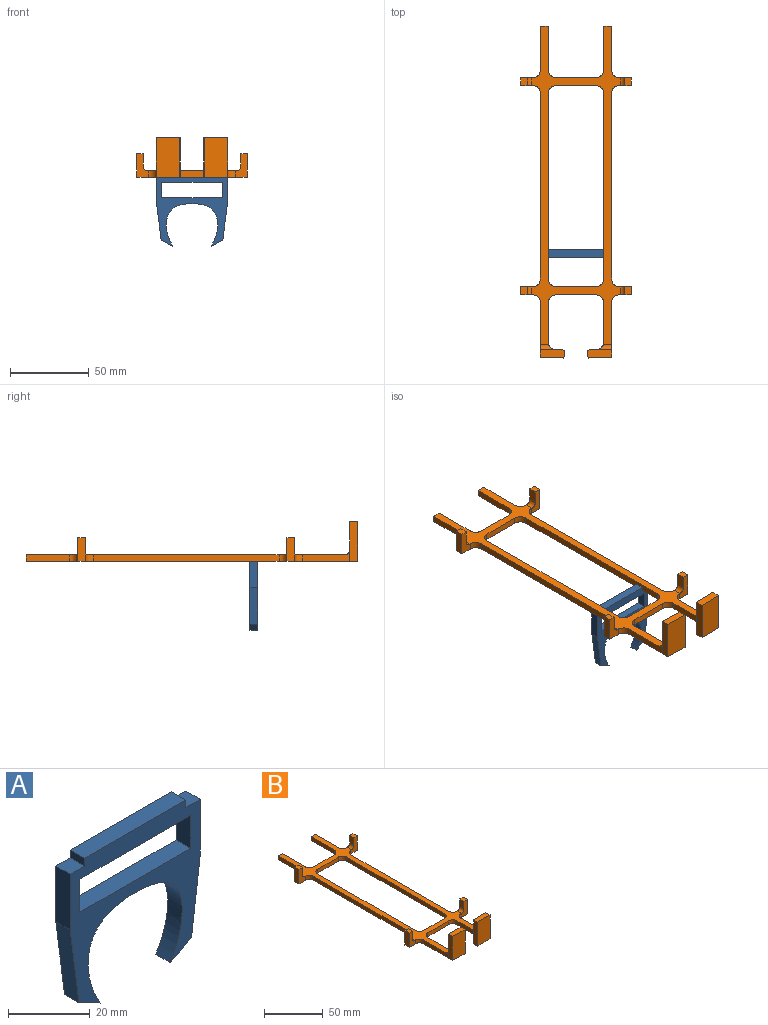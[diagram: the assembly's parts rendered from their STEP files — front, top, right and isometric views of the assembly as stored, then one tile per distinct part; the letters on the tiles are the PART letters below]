
ASSEMBLY  parts=2 mates=1
PART A: 19 faces, bbox 45x5x46.1 mm
  f0: plane 46.06x45mm, normal (0,-1,0), area 782mm2, adj f2,f3,f4,f5,f6,f7,f8,f9
  f1: plane 46.06x45mm, normal (0,1,0), area 782mm2, adj f2,f3,f4,f5,f6,f7,f8,f9
  f2: plane 35x5mm, normal (0,0,1), area 175mm2, adj f0,f1,f12,f13
  f3: plane 23.26x5mm, normal (0.99,0,-0.13), area 117.3mm2, adj f0,f1,f4,f10
  f4: plane 16.71x5mm, normal (1,0,0), area 83.5mm2, adj f0,f1,f3,f14
  f5: plane 16.71x5mm, normal (-1,0,0), area 83.5mm2, adj f0,f1,f6,f11
  f6: plane 23.26x5mm, normal (-0.99,0,-0.13), area 117.3mm2, adj f0,f1,f5,f7
  f7: plane 7.38x5mm, normal (-0.46,0,-0.89), area 41.5mm2, adj f0,f1,f6,f8
  f8: extruded ~27.06x16.25mm, area 192.7mm2, adj f0,f1,f7,f9
  f9: extruded ~27.06x16.25mm, area 192.7mm2, adj f0,f1,f8,f10
  f10: plane 7.38x5mm, normal (0.46,0,-0.89), area 41.5mm2, adj f0,f1,f3,f9
  f11: plane 5x5mm, normal (0,0,1), area 25mm2, adj f0,f1,f5,f12
  f12: plane 5x2.29mm, normal (-1,0,0), area 11.5mm2, adj f0,f1,f2,f11
  f13: plane 5x2.29mm, normal (1,0,0), area 11.5mm2, adj f0,f1,f2,f14
  f14: plane 5x5mm, normal (0,0,1), area 25mm2, adj f0,f1,f4,f13
  f15: plane 38.33x5mm, normal (0,0,1), area 191.6mm2, adj f0,f1,f16,f18
  f16: plane 9.87x5mm, normal (-1,0,0), area 49.3mm2, adj f0,f1,f15,f17
  f17: plane 38.33x5mm, normal (0,0,-1), area 191.6mm2, adj f0,f1,f16,f18
  f18: plane 9.87x5mm, normal (1,0,0), area 49.3mm2, adj f0,f1,f15,f17
PART B: 74 faces, bbox 70x210.4x25 mm
  f0: plane 25x4mm, normal (0,1,0), area 100mm2, adj f26,f27,f56,f66
  f1: plane 117.57x4mm, normal (1,0,0), area 470.3mm2, adj f26,f27,f56,f57
  f2: plane 25x4mm, normal (0,-1,0), area 100mm2, adj f26,f27,f57,f62
  f3: plane 117.57x4mm, normal (-1,0,0), area 470.3mm2, adj f26,f27,f58,f59
  f4: plane 15x7.5mm, normal (0,1,0), area 75.9mm2, adj f26,f27,f44,f45,f46,f55,f59
  f5: plane 15x7.5mm, normal (0,-1,0), area 75.9mm2, adj f26,f27,f44,f45,f46,f55,f72
  f6: plane 29.73x7.03mm, normal (-1,0,0), area 120.7mm2, adj f26,f27,f28,f54,f72
  f7: plane 24.93x4mm, normal (1,0,0), area 99.7mm2, adj f26,f27,f71,f73
  f8: plane 25x4mm, normal (0,-1,0), area 100mm2, adj f26,f27,f69,f71
  f9: plane 24.93x4mm, normal (-1,0,0), area 99.7mm2, adj f26,f27,f69,f70
  f10: plane 29.73x7.03mm, normal (1,0,0), area 120.7mm2, adj f26,f27,f33,f52,f68
  f11: plane 15x7.5mm, normal (0,-1,0), area 75.9mm2, adj f26,f27,f38,f39,f40,f51,f68
  f12: plane 15x7.5mm, normal (0,1,0), area 75.9mm2, adj f26,f27,f38,f39,f40,f51,f67
  f13: plane 117.57x4mm, normal (1,0,0), area 470.3mm2, adj f26,f27,f65,f67
  f14: plane 15x7.5mm, normal (0,-1,0), area 75.9mm2, adj f26,f27,f41,f42,f43,f50,f65
  f15: plane 15x7.5mm, normal (0,1,0), area 75.9mm2, adj f26,f27,f41,f42,f43,f50,f64
  f16: plane 27.73x4mm, normal (1,0,0), area 110.9mm2, adj f17,f26,f27,f64
  f17: plane 5x4mm, normal (0,1,0), area 20mm2, adj f16,f18,f26,f27
  f18: plane 27.73x4mm, normal (-1,0,0), area 110.9mm2, adj f17,f26,f27,f63
  f19: plane 25x4mm, normal (0,1,0), area 100mm2, adj f26,f27,f60,f63
  f20: plane 27.73x4mm, normal (1,0,0), area 110.9mm2, adj f21,f26,f27,f60
  f21: plane 5x4mm, normal (0,1,0), area 20mm2, adj f20,f22,f26,f27
  f22: plane 27.73x4mm, normal (-1,0,0), area 110.9mm2, adj f21,f26,f27,f61
  f23: plane 15x7.5mm, normal (0,1,0), area 75.9mm2, adj f26,f27,f47,f48,f49,f53,f61
  f24: plane 15x7.5mm, normal (0,-1,0), area 75.9mm2, adj f26,f27,f47,f48,f49,f53,f58
  f25: plane 117.57x4mm, normal (-1,0,0), area 470.3mm2, adj f26,f27,f62,f66
  f26: plane 202.12x56mm, normal (0,0,1), area 2566.4mm2, adj f0,f1,f2,f3,f4,f5,f6,f7
  f27: plane 210.35x70mm, normal (0,0,-1), area 2896.1mm2, adj f0,f1,f2,f3,f4,f5,f6,f7
  f28: plane 25x5mm, normal (-1,0.02,0), area 125mm2, adj f6,f27,f30,f31,f32
  f29: plane 25x5mm, normal (1,-0.02,0), area 125mm2, adj f27,f30,f31,f32
  f30: plane 15.11x5.35mm, normal (0,0,1), area 75mm2, adj f28,f29,f31,f32
  f31: plane 25x15mm, normal (-0.02,-1,0), area 375mm2, adj f27,f28,f29,f30
  f32: plane 25x15mm, normal (0.02,1,0), area 305.8mm2, adj f27,f28,f29,f30,f54,f73
  f33: plane 25x5mm, normal (1,0.02,0), area 125mm2, adj f10,f27,f34,f36,f37
  f34: plane 15.11x5.35mm, normal (0,0,1), area 75mm2, adj f33,f35,f36,f37
  f35: plane 25x5mm, normal (-1,-0.02,0), area 125mm2, adj f27,f34,f36,f37
  f36: plane 25x15mm, normal (0.02,-1,0), area 375mm2, adj f27,f33,f34,f35
  f37: plane 25x15mm, normal (-0.02,1,0), area 305.8mm2, adj f27,f33,f34,f35,f52,f70
  f38: plane 8x5mm, normal (-1,0,0), area 40mm2, adj f11,f12,f39,f51
  f39: plane 5x4mm, normal (0,0,1), area 20mm2, adj f11,f12,f38,f40
  f40: plane 15x5mm, normal (1,0,0), area 75mm2, adj f11,f12,f27,f39
  f41: plane 8x5mm, normal (-1,0,0), area 40mm2, adj f14,f15,f42,f50
  f42: plane 5x4mm, normal (0,0,1), area 20mm2, adj f14,f15,f41,f43
  f43: plane 15x5mm, normal (1,0,0), area 75mm2, adj f14,f15,f27,f42
  f44: plane 5x4mm, normal (0,0,1), area 20mm2, adj f4,f5,f45,f46
  f45: plane 15x5mm, normal (-1,0,0), area 75mm2, adj f4,f5,f27,f44
  f46: plane 8x5mm, normal (1,0,0), area 40mm2, adj f4,f5,f44,f55
  f47: plane 5x4mm, normal (0,0,1), area 20mm2, adj f23,f24,f48,f49
  f48: plane 15x5mm, normal (-1,0,0), area 75mm2, adj f23,f24,f27,f47
  f49: plane 8x5mm, normal (1,0,0), area 40mm2, adj f23,f24,f47,f53
  f50: cylinder r=3mm len=5mm, axis (0,-1,0), area 23.6mm2, adj f14,f15,f26,f41
  f51: cylinder r=3mm len=5mm, axis (0,-1,0), area 23.6mm2, adj f11,f12,f26,f38
  f52: cylinder r=3mm len=10.02mm, axis (1,0.02,0), area 34.3mm2, adj f10,f26,f37,f70
  f53: cylinder r=3mm len=5mm, axis (0,-1,0), area 23.6mm2, adj f23,f24,f26,f49
  f54: cylinder r=3mm len=10.02mm, axis (-1,0.02,0), area 34.3mm2, adj f6,f26,f32,f73
  f55: cylinder r=3mm len=5mm, axis (0,-1,0), area 23.6mm2, adj f4,f5,f26,f46
  f56: cylinder r=5mm len=5mm, axis (0,0,1), area 31.4mm2, adj f0,f1,f26,f27
  f57: cylinder r=5mm len=5mm, axis (0,0,-1), area 31.4mm2, adj f1,f2,f26,f27
  f58: cylinder r=5mm len=5mm, axis (0,0,-1), area 31.4mm2, adj f3,f24,f26,f27
  f59: cylinder r=5mm len=5mm, axis (0,0,1), area 31.4mm2, adj f3,f4,f26,f27
  f60: cylinder r=5mm len=5mm, axis (0,0,1), area 31.4mm2, adj f19,f20,f26,f27
  f61: cylinder r=5mm len=5mm, axis (0,0,1), area 31.4mm2, adj f22,f23,f26,f27
  f62: cylinder r=5mm len=5mm, axis (0,0,1), area 31.4mm2, adj f2,f25,f26,f27
  f63: cylinder r=5mm len=5mm, axis (0,0,-1), area 31.4mm2, adj f18,f19,f26,f27
  f64: cylinder r=5mm len=5mm, axis (0,0,-1), area 31.4mm2, adj f15,f16,f26,f27
  f65: cylinder r=5mm len=5mm, axis (0,0,1), area 31.4mm2, adj f13,f14,f26,f27
  f66: cylinder r=5mm len=5mm, axis (0,0,-1), area 31.4mm2, adj f0,f25,f26,f27
  f67: cylinder r=5mm len=5mm, axis (0,0,-1), area 31.4mm2, adj f12,f13,f26,f27
  f68: cylinder r=5mm len=5mm, axis (0,0,1), area 31.4mm2, adj f10,f11,f26,f27
  f69: cylinder r=5mm len=5mm, axis (0,0,1), area 31.4mm2, adj f8,f9,f26,f27
  f70: cylinder r=5mm len=7mm, axis (0,0,-1), area 37.5mm2, adj f9,f26,f27,f37,f52
  f71: cylinder r=5mm len=5mm, axis (0,0,1), area 31.4mm2, adj f7,f8,f26,f27
  f72: cylinder r=5mm len=5mm, axis (0,0,-1), area 31.4mm2, adj f5,f6,f26,f27
  f73: cylinder r=5mm len=7mm, axis (0,0,-1), area 37.5mm2, adj f7,f26,f27,f32,f54
PLACE A t=(-1.44,-25.89,-28.32)mm
PLACE B t=(-1.44,-72.01,4.99)mm fixed
MATE planar B.f13 <-> A.f4  axis (1,0,0) through (21.06,14.49,6.99)mm
